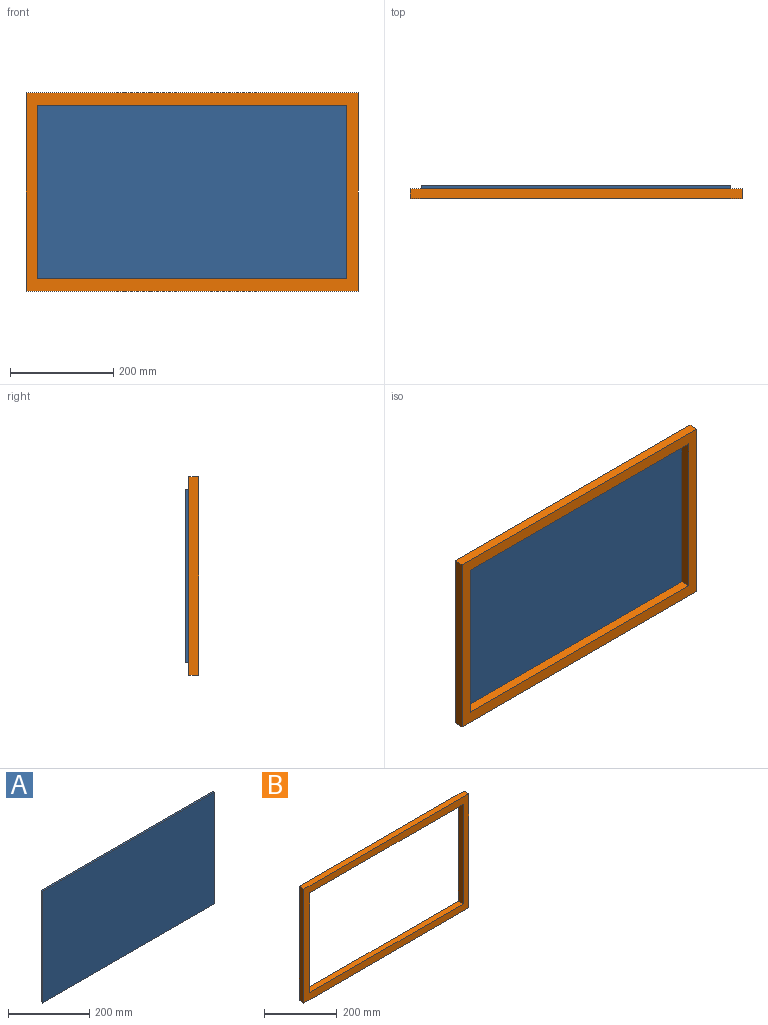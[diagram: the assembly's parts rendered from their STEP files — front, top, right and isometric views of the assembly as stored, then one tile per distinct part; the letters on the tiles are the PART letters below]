
ASSEMBLY  parts=2 mates=1
PART A: 6 faces, bbox 598x6.4x336 mm
  f0: plane 336x6.35mm, normal (-1,0,0), area 2133.6mm2, adj f1,f3,f4,f5
  f1: plane 598x6.35mm, normal (0,0,-1), area 3797.3mm2, adj f0,f2,f4,f5
  f2: plane 336x6.35mm, normal (1,0,0), area 2133.6mm2, adj f1,f3,f4,f5
  f3: plane 598x6.35mm, normal (0,0,1), area 3797.3mm2, adj f0,f2,f4,f5
  f4: plane 598x336mm, normal (0,-1,0), area 200928.1mm2, adj f0,f1,f2,f3
  f5: plane 598x336mm, normal (0,1,0), area 200928.1mm2, adj f0,f1,f2,f3
PART B: 10 faces, bbox 642x19.1x384 mm
  f0: plane 642x384mm, normal (0,-1,0), area 45599.9mm2, adj f2,f3,f4,f5,f6,f7,f8,f9
  f1: plane 642x384mm, normal (0,1,0), area 45599.9mm2, adj f2,f3,f4,f5,f6,f7,f8,f9
  f2: plane 384x19.05mm, normal (-1,0,0), area 7315.2mm2, adj f0,f1,f3,f5
  f3: plane 642x19.05mm, normal (0,0,-1), area 12230.1mm2, adj f0,f1,f2,f4
  f4: plane 384x19.05mm, normal (1,0,0), area 7315.2mm2, adj f0,f1,f3,f5
  f5: plane 642x19.05mm, normal (0,0,1), area 12230.1mm2, adj f0,f1,f2,f4
  f6: plane 336x19.05mm, normal (1,0,0), area 6400.8mm2, adj f0,f1,f7,f9
  f7: plane 598x19.05mm, normal (0,0,1), area 11391.9mm2, adj f0,f1,f6,f8
  f8: plane 336x19.05mm, normal (-1,0,0), area 6400.8mm2, adj f0,f1,f7,f9
  f9: plane 598x19.05mm, normal (0,0,-1), area 11391.9mm2, adj f0,f1,f6,f8
PLACE A t=(-396.14,-269.01,-84.25)mm
PLACE B t=(-396.14,-275.36,-84.25)mm
MATE fastened A.f0 <-> B.f6  axis (-1,0,0) through (-695.14,-275.36,83.75)mm
